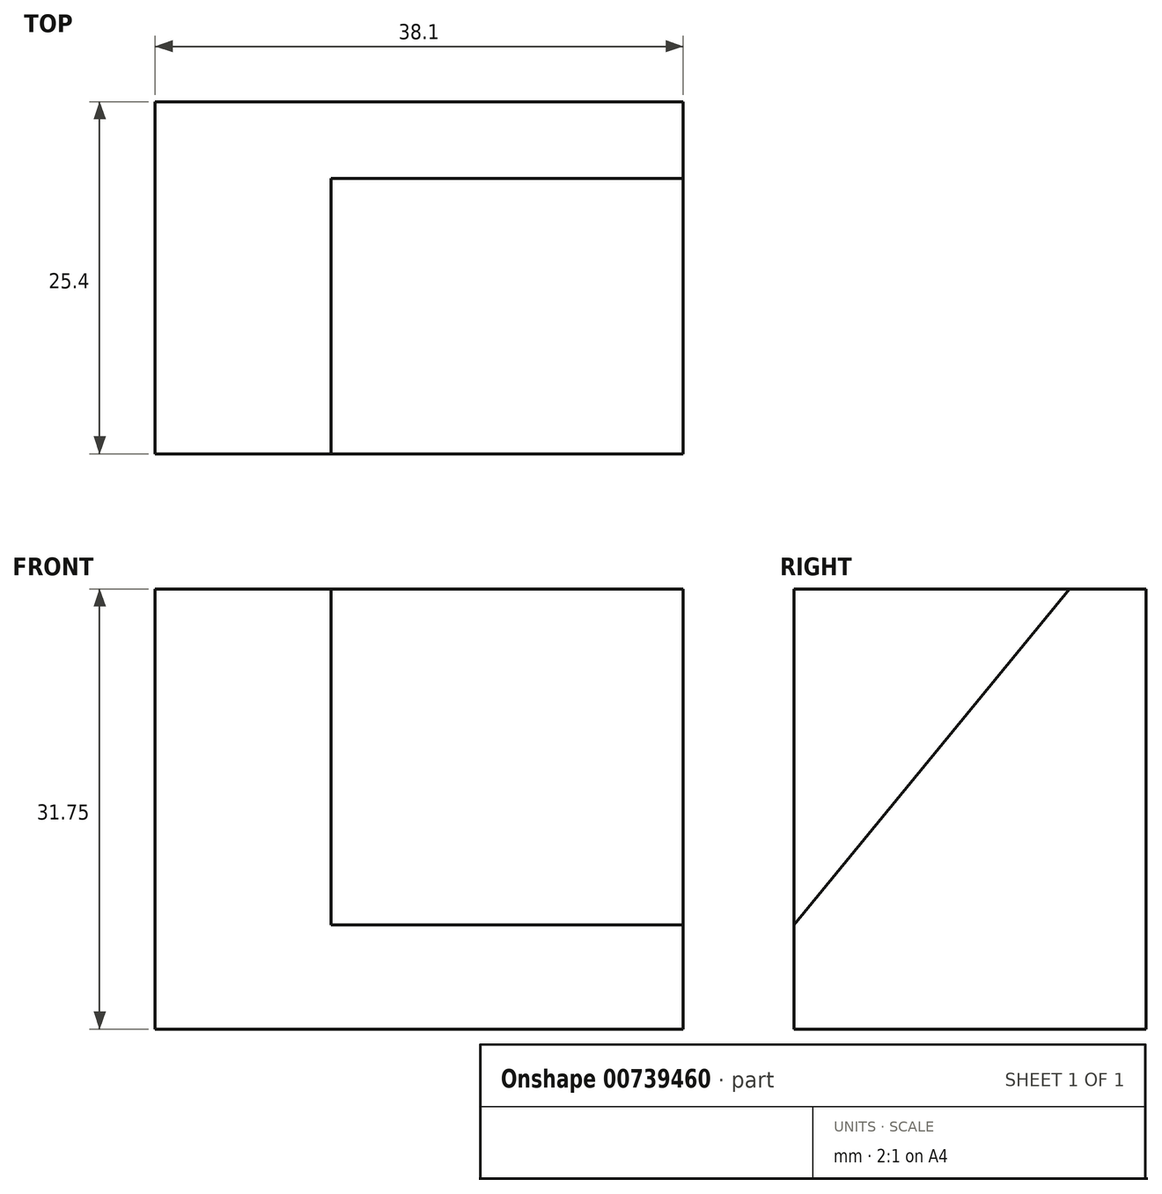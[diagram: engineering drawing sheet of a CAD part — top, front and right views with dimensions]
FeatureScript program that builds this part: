
annotation { "Feature Type Name" : "Feature", "Feature Type Description" : "" }
export const myFeature = defineFeature(function(context is Context, id is Id, definition is map)
    precondition{}
    {
        {
            var Q0;
            Q0=qCreatedBy(makeId("Front.planeOp"),FACE);
            var sketch = newSketch(context, id + "F0", { "sketchPlane" : qUnion([Q0])});
            skLineSegment(sketch, "E0", {"start": v(0, 0) * mm, "end": v(38.1, 0) * mm});
            skLineSegment(sketch, "E1", {"start": v(38.1, 0) * mm, "end": v(38.1, 31.75) * mm});
            skLineSegment(sketch, "E2", {"start": v(38.1, 31.75) * mm, "end": v(0, 31.75) * mm});
            skLineSegment(sketch, "E3", {"start": v(0, 31.75) * mm, "end": v(0, 0) * mm});
            skSolve(sketch);
        }
        {
            var Q0;
            Q0 = qSketchRegion(id + "F0", true);
            extrude(context, id + "F1", {"entities" : qUnion([Q0]), "depth" : 25.4 * mm, "offsetDistance" : 25.4 * mm});
        }
        {
            var Q0;
            Q0=makeQuery(id+"F1.opExtrude","SWEPT_FACE",FACE,{"disambiguationData":[OSD([sQuery(id+"F0.wireOp",EDGE,"E1")])]});
            var sketch = newSketch(context, id + "F2", { "sketchPlane" : qUnion([Q0])});
            skLineSegment(sketch, "E4", {"start": v(-5.53, 31.75) * mm, "end": v(-25.4, 7.52) * mm});
            skLineSegment(sketch, "E5", {"start": v(-25.4, 7.52) * mm, "end": v(-25.4, 31.75) * mm});
            skLineSegment(sketch, "E6", {"start": v(-25.4, 31.75) * mm, "end": v(-5.53, 31.75) * mm});
            skSolve(sketch);
        }
        {
            var Q0;
            Q0=makeQuery(id+"F2.imprint","IMPRINT",FACE,{"disambiguationData":[TD([[makeQuery(id+"F2.imprint","IMPRINT",EDGE,{"derivedFrom":sQuery(id+"F2.wireOp",EDGE,"E4")}),-1.0]])]});
            extrude(context, id + "F3", {"entities" : qUnion([Q0]), "operationType" : NewBodyOperationType.REMOVE, "oppositeDirection" : true, "depth" : 25.4 * mm, "offsetDistance" : 25.4 * mm});
        }
    });
